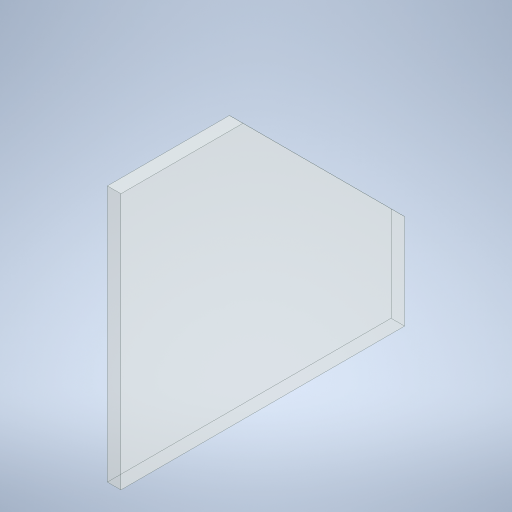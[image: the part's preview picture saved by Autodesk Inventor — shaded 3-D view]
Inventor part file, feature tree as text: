
AUTODESK INVENTOR PART (.ipt)
format: ipt  version: 2024 (Build 280153000, 153)  size: 229,376 bytes
history: native  units: in
note: dims shown in document units (in); Inventor stores cm internally (conversion verified against a paired STEP export)
features: extrude x1, sketch x1
ambient origin geometry x8: Origin, YZ Plane, XZ Plane, XY Plane, X Axis, Y Axis, Z Axis, Center Point
bodies: Solid1 (feature_tree)
feature tree (2):
  extrude  "Extrusion1"  Depth=0.75in
  sketch  "Sketch1"  dims[d0=105.287in d1=96.0in d2=36.0in d3=135.0deg d4=5.0in d5=0.0in d6=0.75in d7=0.75in d8=0.75in]
